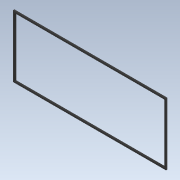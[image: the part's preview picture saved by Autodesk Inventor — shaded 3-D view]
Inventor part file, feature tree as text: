
AUTODESK INVENTOR PART (.ipt)
format: ipt  version: 2020 (Build 240168000, 168)  size: 99,840 bytes
history: native  units: mm
features: extrude x1, fillet x1, sketch x1
ambient origin geometry x8: Origin, YZ Plane, XZ Plane, XY Plane, X Axis, Y Axis, Z Axis, Center Point
bodies: Volumenkörper1 (feature_tree)
feature tree (3):
  extrude  "Extrusion1"  Depth=107.0mm
  fillet  "Rundung1"  Radius=3.0mm
  sketch  "Skizze1"  dims[d0=272.0mm d1=107.0mm d2=3.0mm d3=3.0mm d4=3.0mm d5=3.0mm d6=3.0mm d7=0.0mm d8=1.0mm]
